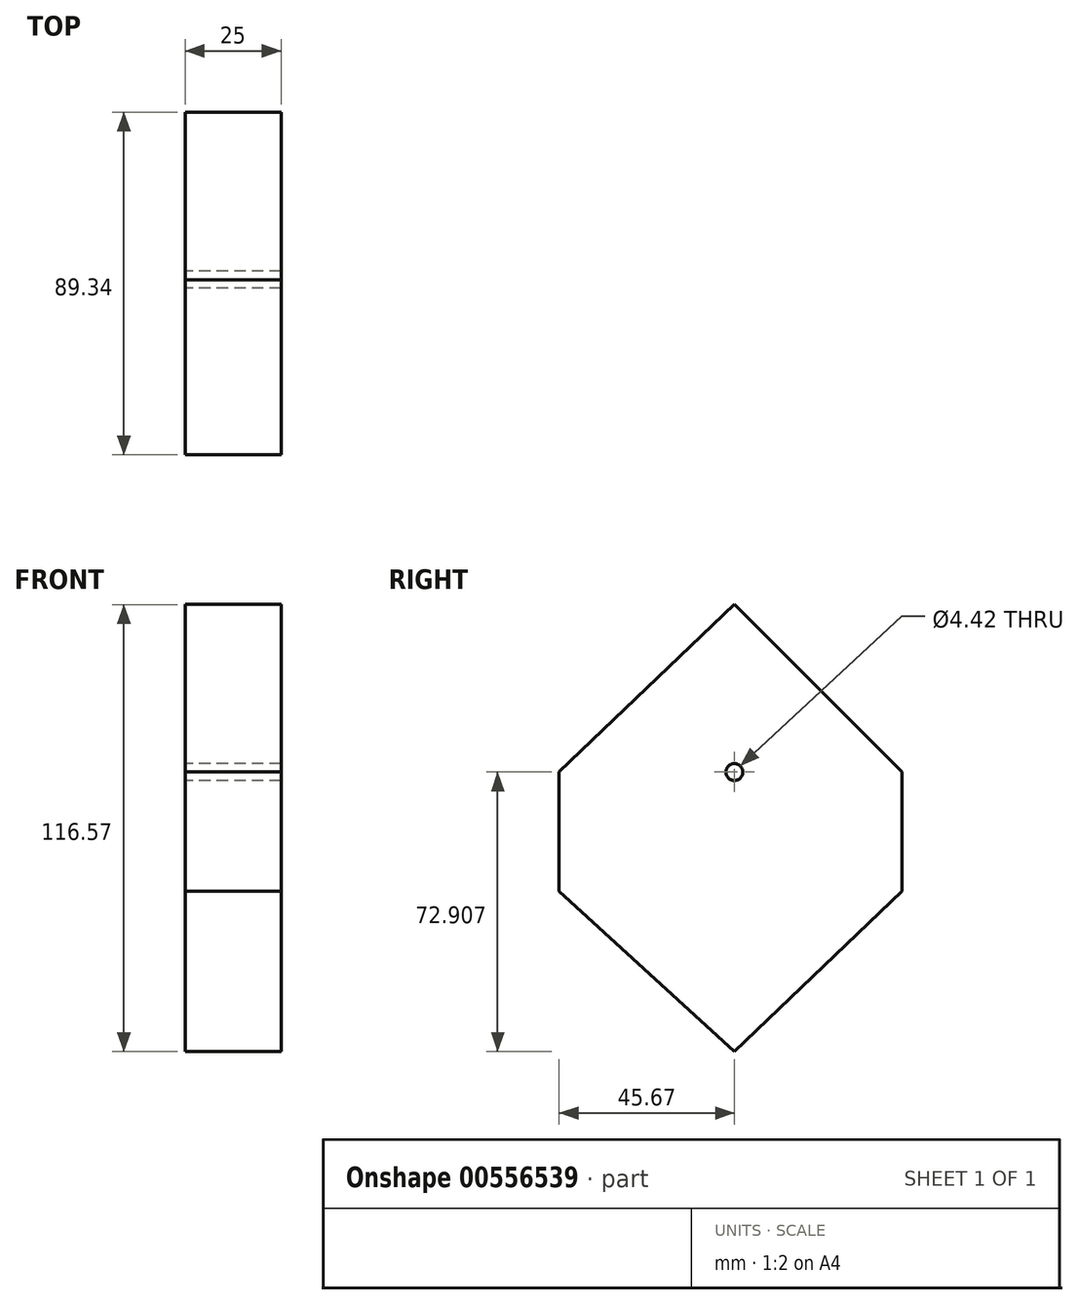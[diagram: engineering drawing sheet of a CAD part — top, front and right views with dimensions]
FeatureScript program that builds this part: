
annotation { "Feature Type Name" : "Feature", "Feature Type Description" : "" }
export const myFeature = defineFeature(function(context is Context, id is Id, definition is map)
    precondition{}
    {
        {
            var Q0;
            Q0=qCreatedBy(makeId("Right.planeOp"),FACE);
            var sketch = newSketch(context, id + "F0", { "sketchPlane" : qUnion([Q0])});
            skLineSegment(sketch, "E0", {"start": v(-45.67, 0) * mm, "end": v(-45.67, 31.05) * mm});
            skLineSegment(sketch, "E1", {"start": v(43.67, 0) * mm, "end": v(43.67, 31.05) * mm});
            skLineSegment(sketch, "E2", {"start": v(43.67, 31.05) * mm, "end": v(-45.67, 31.05) * mm});
            skLineSegment(sketch, "E3", {"start": v(-45.67, 0) * mm, "end": v(43.67, 0) * mm});
            skLineSegment(sketch, "E4", {"start": v(-45.67, 0) * mm, "end": v(0, -41.86) * mm});
            skLineSegment(sketch, "E5", {"start": v(0, -41.86) * mm, "end": v(43.67, 0) * mm});
            skLineSegment(sketch, "E6", {"start": v(-45.67, 31.05) * mm, "end": v(0, 74.71) * mm});
            skLineSegment(sketch, "E7", {"start": v(0, 74.71) * mm, "end": v(43.67, 31.05) * mm});
            skCircle(sketch, "E8", {"center": v(0, 31.05) * mm, "radius": 2.21 * mm});
            skPoint(sketch, "E8.centerSnap0", {"position": v(-1, 31.05) * mm});
            skSolve(sketch);
        }
        {
            var Q0;
            Q0=makeQuery(id+"F0.imprint","IMPRINT",FACE,{"disambiguationData":[TD([[makeQuery(id+"F0.imprint","IMPRINT",EDGE,{"derivedFrom":sQuery(id+"F0.wireOp",EDGE,"E0")}),-1.0]])]});
            var Q1;
            Q1=makeQuery(id+"F0.imprint","IMPRINT",FACE,{"disambiguationData":[TD([[makeQuery(id+"F0.imprint","IMPRINT",EDGE,{"derivedFrom":sQuery(id+"F0.wireOp",EDGE,"E3")}),-1.0]])]});
            extrude(context, id + "F1", {"entities" : qUnion([Q0, Q1]), "depth" : 25 * mm, "offsetDistance" : 25 * mm});
        }
        {
            var Q0;
            Q0 = qSketchRegion(id + "F0", true);
            extrude(context, id + "F2", {"entities" : qUnion([Q0]), "operationType" : NewBodyOperationType.ADD, "depth" : 25 * mm, "offsetDistance" : 25 * mm});
        }
    });
